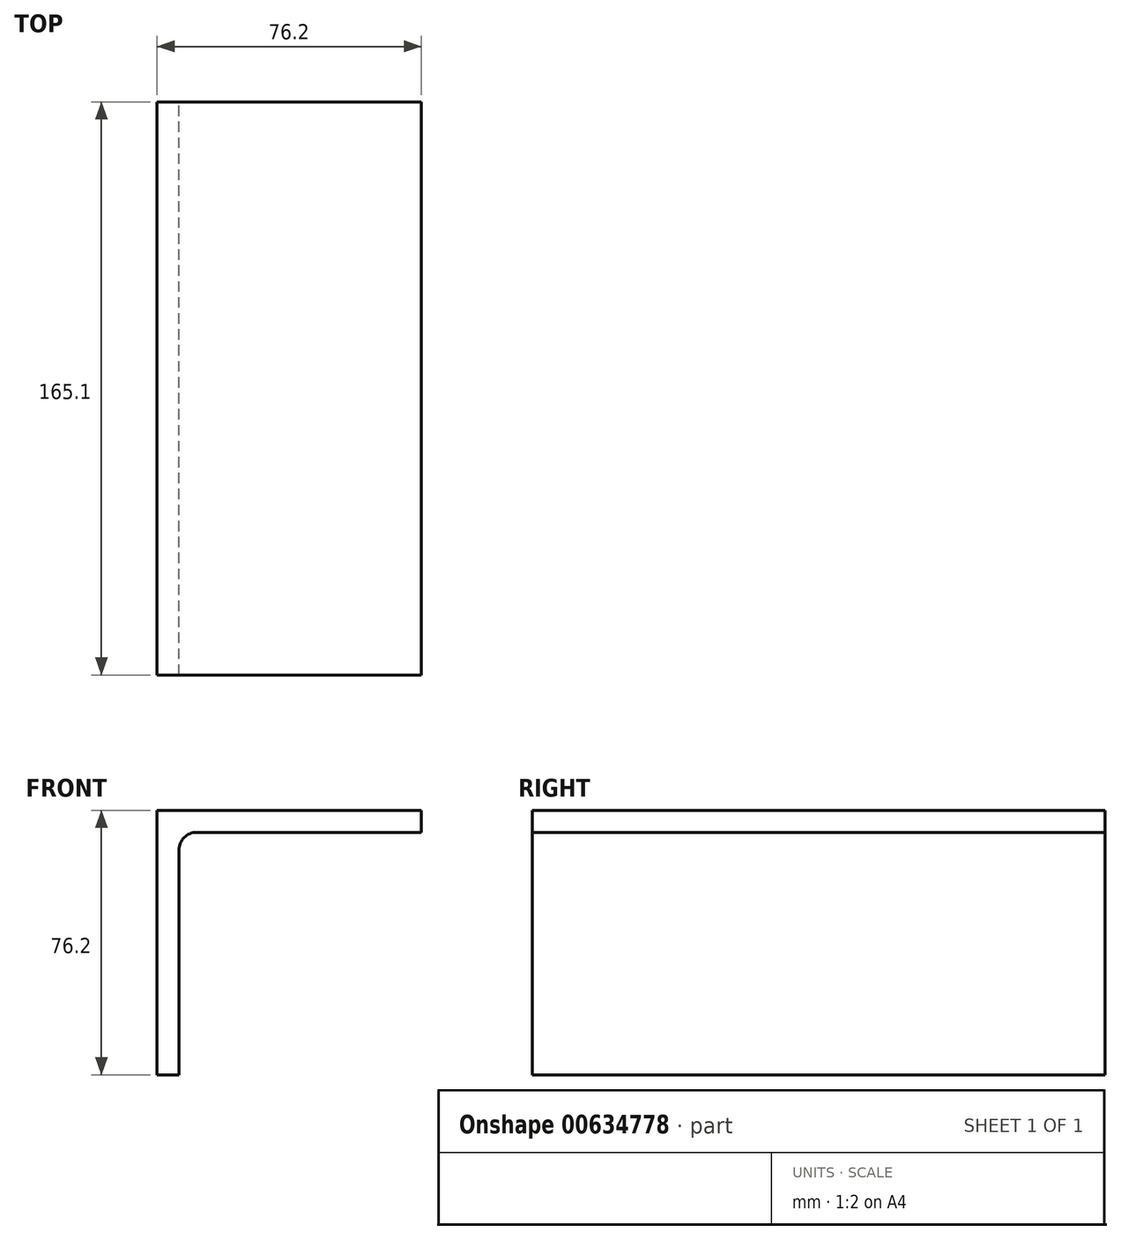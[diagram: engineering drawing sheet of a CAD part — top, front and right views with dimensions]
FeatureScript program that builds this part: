
annotation { "Feature Type Name" : "Feature", "Feature Type Description" : "" }
export const myFeature = defineFeature(function(context is Context, id is Id, definition is map)
    precondition{}
    {
        {
            var Q0;
            Q0=qCreatedBy(makeId("Front.planeOp"),FACE);
            var sketch = newSketch(context, id + "F0", { "sketchPlane" : qUnion([Q0])});
            skLineSegment(sketch, "E0.bottom", {"start": v(0, 0) * mm, "end": v(6.35, 0) * mm});
            skLineSegment(sketch, "E0.top", {"start": v(0, 76.2) * mm, "end": v(76.2, 76.2) * mm});
            skLineSegment(sketch, "E0.left", {"start": v(0, 0) * mm, "end": v(0, 76.2) * mm});
            skLineSegment(sketch, "E1.0", {"start": v(6.35, 69.85) * mm, "end": v(76.2, 69.85) * mm});
            skLineSegment(sketch, "E2.0", {"start": v(6.35, 0) * mm, "end": v(6.35, 69.85) * mm});
            skLineSegment(sketch, "E3", {"start": v(76.2, 76.2) * mm, "end": v(76.2, 69.85) * mm});
            skSolve(sketch);
        }
        {
            var Q0;
            Q0 = qSketchRegion(id + "F0", true);
            extrude(context, id + "F1", {"entities" : qUnion([Q0]), "depth" : 165.1 * mm, "offsetDistance" : 25.4 * mm});
        }
        {
            var Q0;
            Q0=makeQuery(id+"F1.opExtrude","SWEPT_EDGE",EDGE,{"disambiguationData":[OSD([sQuery(id+"F0.wireOp",EDGE,"E1.0"),sQuery(id+"F0.wireOp",EDGE,"E2.0")])]});
            fillet(context, id + "F2", {"entities" : qUnion([Q0]), "radius" : 5.08 * mm, "tangentPropagation" : true, "allowEdgeOverflow" : false});
        }
    });
